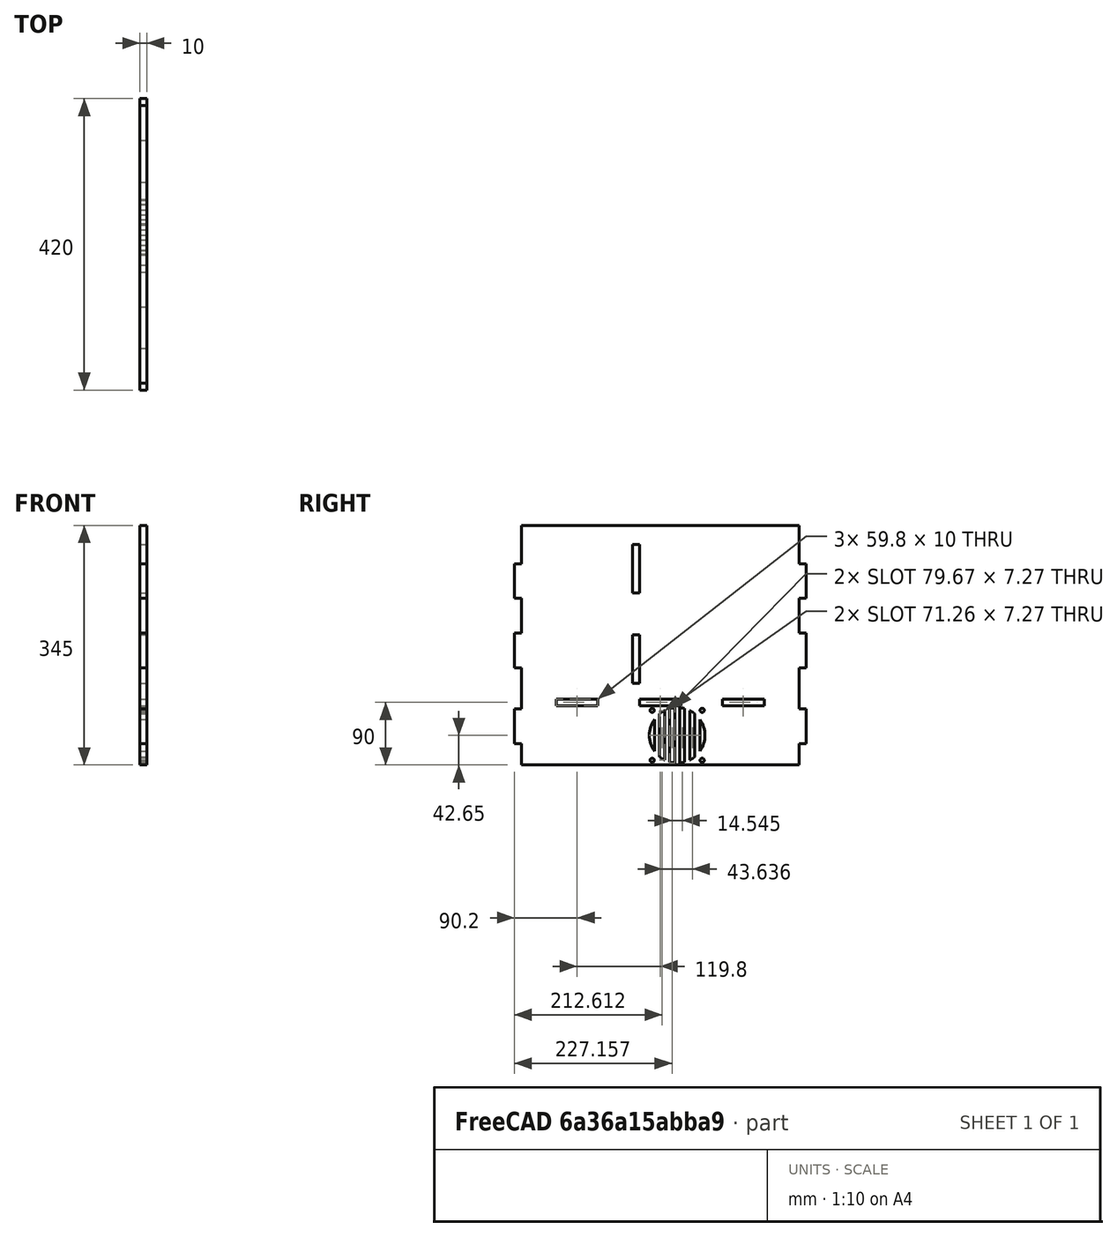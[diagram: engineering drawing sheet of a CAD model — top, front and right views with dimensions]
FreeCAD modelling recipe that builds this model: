
FCSTD DOCUMENT  (FreeCAD 0.19R19327 (Git))
Label: Trasera
License: All rights reserved
LicenseURL: http://en.wikipedia.org/wiki/All_rights_reserved
objects: Sketcher::SketchObject×1, PartDesign::Pad×1, PartDesign::Body×1
note: 4 computed .brp shape members not serialized (recipe doc carries the construction recipe); baked Part::Feature solids carry a one-line shape summary decoded from their .brp

FEATURE [Sketcher::SketchObject] Sketch
  MapMode = 5
  Placement = pos=(0,0,0) rot=(0.57735,0.57735,0.57735;2.0944rad)
  Support = -> [YZ_Plane]
  sketch-geometry (93):
    g0: LineSegment StartX=0 StartY=0 StartZ=0 EndX=0 EndY=30.83 EndZ=0
    g1: LineSegment StartX=0 StartY=30.83 StartZ=0 EndX=-10 EndY=30.83 EndZ=0
    g2: LineSegment StartX=-10 StartY=30.83 StartZ=0 EndX=-10 EndY=80.83 EndZ=0
    g3: LineSegment StartX=-10 StartY=80.83 StartZ=0 EndX=0 EndY=80.83 EndZ=0
    g4: LineSegment StartX=0 StartY=80.83 StartZ=0 EndX=0 EndY=140.1 EndZ=0
    g5: LineSegment StartX=0 StartY=140.1 StartZ=0 EndX=-10 EndY=140.1 EndZ=0
    g6: LineSegment StartX=-10 StartY=140.1 StartZ=0 EndX=-10 EndY=190.1 EndZ=0
    g7: LineSegment StartX=-10 StartY=190.1 StartZ=0 EndX=0 EndY=190.1 EndZ=0
    g8: LineSegment StartX=0 StartY=190.1 StartZ=0 EndX=0 EndY=239.9 EndZ=0
    g9: LineSegment StartX=0 StartY=239.9 StartZ=0 EndX=-10 EndY=239.9 EndZ=0
    g10: LineSegment StartX=-10 StartY=239.9 StartZ=0 EndX=-10 EndY=289.9 EndZ=0
    g11: LineSegment StartX=-10 StartY=289.9 StartZ=0 EndX=0 EndY=289.9 EndZ=0
    g12: LineSegment StartX=0 StartY=289.9 StartZ=0 EndX=0 EndY=345 EndZ=0
    g13: LineSegment StartX=0 StartY=345 StartZ=0 EndX=400 EndY=345 EndZ=0
    g14: LineSegment StartX=400 StartY=345 StartZ=0 EndX=400 EndY=289.9 EndZ=0
    g15: LineSegment StartX=400 StartY=289.9 StartZ=0 EndX=410 EndY=289.9 EndZ=0
    g16: LineSegment StartX=410 StartY=289.9 StartZ=0 EndX=410 EndY=239.9 EndZ=0
    g17: LineSegment StartX=410 StartY=239.9 StartZ=0 EndX=400 EndY=239.9 EndZ=0
    g18: LineSegment StartX=400 StartY=239.9 StartZ=0 EndX=400 EndY=190.1 EndZ=0
    g19: LineSegment StartX=400 StartY=190.1 StartZ=0 EndX=410 EndY=190.1 EndZ=0
    g20: LineSegment StartX=410 StartY=190.1 StartZ=0 EndX=410 EndY=140.1 EndZ=0
    g21: LineSegment StartX=410 StartY=140.1 StartZ=0 EndX=400 EndY=140.1 EndZ=0
    g22: LineSegment StartX=400 StartY=140.1 StartZ=0 EndX=400 EndY=80.83 EndZ=0
    g23: LineSegment StartX=400 StartY=80.83 StartZ=0 EndX=410 EndY=80.83 EndZ=0
    g24: LineSegment StartX=410 StartY=80.83 StartZ=0 EndX=410 EndY=30.83 EndZ=0
    g25: LineSegment StartX=410 StartY=30.83 StartZ=0 EndX=400 EndY=30.83 EndZ=0
    g26: LineSegment StartX=400 StartY=30.83 StartZ=0 EndX=400 EndY=0 EndZ=0
    g27: LineSegment StartX=400 StartY=0 StartZ=0 EndX=0 EndY=0 EndZ=0
    g28: LineSegment StartX=50.3 StartY=95 StartZ=0 EndX=110.1 EndY=95 EndZ=0
    g29: LineSegment StartX=110.1 StartY=95 StartZ=0 EndX=110.1 EndY=85 EndZ=0
    g30: LineSegment StartX=110.1 StartY=85 StartZ=0 EndX=50.3 EndY=85 EndZ=0
    g31: LineSegment StartX=50.3 StartY=85 StartZ=0 EndX=50.3 EndY=95 EndZ=0
    g32: LineSegment StartX=170.1 StartY=95 StartZ=0 EndX=229.9 EndY=95 EndZ=0
    g33: LineSegment StartX=229.9 StartY=95 StartZ=0 EndX=229.9 EndY=85 EndZ=0
    g34: LineSegment StartX=229.9 StartY=85 StartZ=0 EndX=170.1 EndY=85 EndZ=0
    g35: LineSegment StartX=170.1 StartY=85 StartZ=0 EndX=170.1 EndY=95 EndZ=0
    g36: LineSegment StartX=289.9 StartY=95 StartZ=0 EndX=349.7 EndY=95 EndZ=0
    g37: LineSegment StartX=349.7 StartY=95 StartZ=0 EndX=349.7 EndY=85 EndZ=0
    g38: LineSegment StartX=349.7 StartY=85 StartZ=0 EndX=289.9 EndY=85 EndZ=0
    g39: LineSegment StartX=289.9 StartY=85 StartZ=0 EndX=289.9 EndY=95 EndZ=0
    g40: LineSegment [constr] StartX=-5e-16 StartY=85 StartZ=0 EndX=50.3 EndY=85 EndZ=0
    g41: LineSegment [constr] StartX=110.1 StartY=85 StartZ=0 EndX=170.1 EndY=85 EndZ=0
    g42: LineSegment [constr] StartX=229.9 StartY=85 StartZ=0 EndX=289.9 EndY=85 EndZ=0
    g43: LineSegment [constr] StartX=349.7 StartY=85 StartZ=0 EndX=400 EndY=85 EndZ=0
    g44: LineSegment StartX=160 StartY=317.4 StartZ=0 EndX=170 EndY=317.4 EndZ=0
    g45: LineSegment StartX=170 StartY=317.4 StartZ=0 EndX=170 EndY=247.6 EndZ=0
    g46: LineSegment StartX=170 StartY=247.6 StartZ=0 EndX=160 EndY=247.6 EndZ=0
    g47: LineSegment StartX=160 StartY=247.6 StartZ=0 EndX=160 EndY=317.4 EndZ=0
    g48: LineSegment StartX=160 StartY=187.4 StartZ=0 EndX=170 EndY=187.4 EndZ=0
    g49: LineSegment StartX=170 StartY=187.4 StartZ=0 EndX=170 EndY=117.6 EndZ=0
    g50: LineSegment StartX=170 StartY=117.6 StartZ=0 EndX=160 EndY=117.6 EndZ=0
    g51: LineSegment StartX=160 StartY=117.6 StartZ=0 EndX=160 EndY=187.4 EndZ=0
    g52: LineSegment [constr] StartX=160 StartY=187.4 StartZ=0 EndX=160 EndY=247.6 EndZ=0
    g53: LineSegment [constr] StartX=188.43 StartY=78.65 StartZ=0 EndX=260.43 EndY=78.65 EndZ=0
    g54: LineSegment [constr] StartX=260.43 StartY=78.65 StartZ=0 EndX=260.43 EndY=6.65 EndZ=0
    g55: LineSegment [constr] StartX=260.43 StartY=6.65 StartZ=0 EndX=188.43 EndY=6.65 EndZ=0
    g56: LineSegment [constr] StartX=188.43 StartY=6.65 StartZ=0 EndX=188.43 EndY=78.65 EndZ=0
    g57: Circle CenterX=188.43 CenterY=6.65 CenterZ=0 NormalX=0 NormalY=0 NormalZ=1 AngleXU=0 Radius=3
    g58: Circle CenterX=260.43 CenterY=6.65 CenterZ=0 NormalX=0 NormalY=0 NormalZ=1 AngleXU=0 Radius=3
    g59: Circle CenterX=260.43 CenterY=78.65 CenterZ=0 NormalX=0 NormalY=0 NormalZ=1 AngleXU=0 Radius=3
    g60: Circle CenterX=188.43 CenterY=78.65 CenterZ=0 NormalX=0 NormalY=0 NormalZ=1 AngleXU=0 Radius=3
    g61: LineSegment [constr] StartX=188.43 StartY=6.65 StartZ=0 EndX=260.43 EndY=78.65 EndZ=0
    g62: ArcOfCircle CenterX=224.43 CenterY=42.65 CenterZ=0 NormalX=0 NormalY=0 NormalZ=1 AngleXU=0 Radius=40 StartAngle=2.52904 EndAngle=3.75415
    g63: LineSegment StartX=191.703 StartY=19.6516 StartZ=0 EndX=191.703 EndY=65.6484 EndZ=0
    g64: LineSegment StartX=198.975 StartY=11.7944 StartZ=0 EndX=198.975 EndY=73.5056 EndZ=0
    g65: LineSegment StartX=206.248 StartY=7.02106 StartZ=0 EndX=206.248 EndY=78.2789 EndZ=0
    g66: LineSegment StartX=213.521 StartY=4.16634 StartZ=0 EndX=213.521 EndY=81.1337 EndZ=0
    g67: LineSegment StartX=220.794 StartY=2.81563 StartZ=0 EndX=220.794 EndY=82.4844 EndZ=0
    g68: LineSegment [constr] StartX=206.248 StartY=42.65 StartZ=0 EndX=213.521 EndY=42.65 EndZ=0
    g69: LineSegment [constr] StartX=220.794 StartY=42.65 StartZ=0 EndX=228.066 EndY=42.65 EndZ=0
    g70: LineSegment [constr] StartX=191.703 StartY=42.65 StartZ=0 EndX=198.975 EndY=42.65 EndZ=0
    g71: LineSegment StartX=228.066 StartY=2.81563 StartZ=0 EndX=228.066 EndY=82.4844 EndZ=0
    g72: LineSegment StartX=235.339 StartY=4.16634 StartZ=0 EndX=235.339 EndY=81.1337 EndZ=0
    g73: LineSegment StartX=242.612 StartY=7.02106 StartZ=0 EndX=242.612 EndY=78.2789 EndZ=0
    g74: LineSegment StartX=249.885 StartY=73.5056 StartZ=0 EndX=249.885 EndY=11.7944 EndZ=0
    g75: LineSegment StartX=257.157 StartY=19.6516 StartZ=0 EndX=257.157 EndY=65.6484 EndZ=0
    g76: LineSegment [constr] StartX=235.339 StartY=42.65 StartZ=0 EndX=242.612 EndY=42.65 EndZ=0
    g77: LineSegment [constr] StartX=249.885 StartY=42.65 StartZ=0 EndX=257.157 EndY=42.65 EndZ=0
    g78: LineSegment [constr] StartX=184.43 StartY=42.65 StartZ=0 EndX=191.703 EndY=42.65 EndZ=0
    g79: LineSegment [constr] StartX=198.975 StartY=42.65 StartZ=0 EndX=206.248 EndY=42.65 EndZ=0
    g80: LineSegment [constr] StartX=213.521 StartY=42.65 StartZ=0 EndX=220.794 EndY=42.65 EndZ=0
    g81: LineSegment [constr] StartX=228.066 StartY=42.65 StartZ=0 EndX=235.339 EndY=42.65 EndZ=0
    g82: LineSegment [constr] StartX=242.612 StartY=42.65 StartZ=0 EndX=249.885 EndY=42.65 EndZ=0
    g83: LineSegment [constr] StartX=257.157 StartY=42.65 StartZ=0 EndX=264.43 EndY=42.65 EndZ=0
    g84: ArcOfCircle CenterX=224.43 CenterY=42.65 CenterZ=0 NormalX=0 NormalY=0 NormalZ=1 AngleXU=0 Radius=40 StartAngle=4.02261 EndAngle=4.24053
    g85: ArcOfCircle CenterX=224.43 CenterY=42.65 CenterZ=0 NormalX=0 NormalY=0 NormalZ=1 AngleXU=0 Radius=40 StartAngle=4.43616 EndAngle=4.62135
    g86: ArcOfCircle CenterX=224.43 CenterY=42.65 CenterZ=0 NormalX=0 NormalY=0 NormalZ=1 AngleXU=0 Radius=40 StartAngle=2.04266 EndAngle=2.26057
    g87: ArcOfCircle CenterX=224.43 CenterY=42.65 CenterZ=0 NormalX=0 NormalY=0 NormalZ=1 AngleXU=0 Radius=40 StartAngle=1.66183 EndAngle=1.84702
    g88: ArcOfCircle CenterX=224.43 CenterY=42.65 CenterZ=0 NormalX=0 NormalY=0 NormalZ=1 AngleXU=0 Radius=40 StartAngle=4.80342 EndAngle=4.98862
    g89: ArcOfCircle CenterX=224.43 CenterY=42.65 CenterZ=0 NormalX=0 NormalY=0 NormalZ=1 AngleXU=0 Radius=40 StartAngle=5.18425 EndAngle=5.40216
    g90: ArcOfCircle CenterX=224.43 CenterY=42.65 CenterZ=0 NormalX=0 NormalY=0 NormalZ=1 AngleXU=0 Radius=40 StartAngle=5.67063 EndAngle=6.89574
    g91: ArcOfCircle CenterX=224.43 CenterY=42.65 CenterZ=0 NormalX=0 NormalY=0 NormalZ=1 AngleXU=0 Radius=40 StartAngle=0.881021 EndAngle=1.09893
    g92: ArcOfCircle CenterX=224.43 CenterY=42.65 CenterZ=0 NormalX=0 NormalY=0 NormalZ=1 AngleXU=0 Radius=40 StartAngle=1.29457 EndAngle=1.47976
  constraints (286):
    c: Coincident(g-1,g0)
    c: PointOnObject(g0,g-2)
    c: Coincident(g0,g1)
    c: Horizontal(g1)
    c: Coincident(g1,g2)
    c: Vertical(g2)
    c: Coincident(g2,g3)
    c: Horizontal(g3)
    c: Coincident(g3,g4)
    c: Vertical(g4)
    c: Coincident(g4,g5)
    c: Coincident(g5,g6)
    c: Vertical(g6)
    c: Coincident(g6,g7)
    c: Horizontal(g7)
    c: Coincident(g7,g8)
    c: Vertical(g8)
    c: Coincident(g8,g9)
    c: Horizontal(g9)
    c: Coincident(g9,g10)
    c: Vertical(g10)
    c: Coincident(g10,g11)
    c: Horizontal(g11)
    c: Coincident(g11,g12)
    c: PointOnObject(g12,g-2)
    c: Coincident(g12,g13)
    c: Horizontal(g13)
    c: Coincident(g13,g14)
    c: Vertical(g14)
    c: Coincident(g14,g15)
    c: Coincident(g15,g16)
    c: Vertical(g16)
    c: Coincident(g16,g17)
    c: Horizontal(g17)
    c: Coincident(g17,g18)
    c: Vertical(g18)
    c: Coincident(g18,g19)
    c: Coincident(g19,g20)
    c: Coincident(g20,g21)
    c: Coincident(g21,g22)
    c: Vertical(g22)
    c: Coincident(g22,g23)
    c: Coincident(g23,g24)
    c: Vertical(g24)
    c: Coincident(g24,g25)
    c: Coincident(g25,g26)
    c: PointOnObject(g26,g-1)
    c: Vertical(g26)
    c: Coincident(g26,g27)
    c: Coincident(g27,g0)
    c: Horizontal(g5)
    c: Equal(g1,g3)
    c: Equal(g3,g5)
    c: Equal(g5,g7)
    c: Equal(g7,g9)
    c: Equal(g9,g11)
    c: Equal(g11,g15)
    c: Equal(g15,g17)
    c: Equal(g17,g19)
    c: Equal(g19,g21)
    c: Equal(g21,g23)
    c: Equal(g23,g25)
    c: Horizontal(g25)
    c: Horizontal(g23)
    c: Horizontal(g21)
    c: Vertical(g20)
    c: Horizontal(g15)
    c: DistanceX(g1,g1) = 10
    c: Equal(g2,g6)
    c: Equal(g6,g10)
    c: Equal(g10,g24)
    c: Equal(g24,g20)
    c: Equal(g20,g16)
    c: DistanceY(g2,g2) = 50
    c: DistanceY(g12,g12) = 55.1
    c: Equal(g12,g14)
    c: Equal(g0,g26)
    c: DistanceY(g0,g0) = 30.83
    c: DistanceX(g13,g13) = 400
    c: DistanceY(g4,g4) = 59.27
    c: Coincident(g28,g29)
    c: Coincident(g29,g30)
    c: Coincident(g30,g31)
    c: Coincident(g31,g28)
    c: Horizontal(g28)
    c: Horizontal(g30)
    c: Vertical(g29)
    c: Vertical(g31)
    c: Coincident(g32,g33)
    c: Coincident(g33,g34)
    c: Coincident(g34,g35)
    c: Coincident(g35,g32)
    c: Horizontal(g32)
    c: Horizontal(g34)
    c: Vertical(g33)
    c: Vertical(g35)
    c: Coincident(g36,g37)
    c: Coincident(g37,g38)
    c: Coincident(g38,g39)
    c: Coincident(g39,g36)
    c: Horizontal(g36)
    c: Horizontal(g38)
    c: Vertical(g37)
    c: Vertical(g39)
    c: Equal(g28,g32)
    c: Equal(g32,g36)
    c: Equal(g39,g35)
    c: Equal(g35,g31)
    c: PointOnObject(g40,g4)
    c: Horizontal(g40)
    c: Coincident(g30,g40)
    c: Coincident(g41,g29)
    c: Horizontal(g41)
    c: Coincident(g34,g41)
    c: Coincident(g42,g33)
    c: Horizontal(g42)
    c: Coincident(g38,g42)
    c: Coincident(g43,g37)
    c: PointOnObject(g43,g22)
    c: Horizontal(g43)
    c: Equal(g43,g40)
    c: Equal(g41,g42)
    c: Coincident(g44,g45)
    c: Coincident(g45,g46)
    c: Coincident(g46,g47)
    c: Coincident(g47,g44)
    c: Horizontal(g44)
    c: Horizontal(g46)
    c: Vertical(g45)
    c: Vertical(g47)
    c: Coincident(g48,g49)
    c: Coincident(g49,g50)
    c: Coincident(g50,g51)
    c: Coincident(g51,g48)
    c: Horizontal(g48)
    c: Horizontal(g50)
    c: Vertical(g49)
    c: Equal(g51,g47)
    c: Equal(g44,g48)
    c: Equal(g31,g50)
    c: Equal(g50,g46)
    c: DistanceX(g48,g48) = 10
    c: DistanceX(g28,g28) = 59.8
    c: DistanceX(g40,g40) = 50.3
    c: DistanceY(g0,g30) = 85
    c: Coincident(g52,g48)
    c: Vertical(g52)
    c: Coincident(g46,g52)
    c: DistanceY(g52,g52) = 60.2
    c: DistanceY(g51,g51) = 69.8
    c: DistanceY(g0,g50) = 117.6
    c: DistanceX(g0,g50) = 160
    c: Coincident(g53,g54)
    c: Coincident(g54,g55)
    c: Coincident(g55,g56)
    c: Coincident(g56,g53)
    c: Horizontal(g53)
    c: Horizontal(g55)
    c: Vertical(g54)
    c: Vertical(g56)
    c: Equal(g55,g54)
    c: DistanceX(g55,g55) = 72
    c: Coincident(g57,g55)
    c: Coincident(g58,g54)
    c: Coincident(g59,g53)
    c: Coincident(g60,g53)
    c: Equal(g60,g59)
    c: Equal(g59,g57)
    c: Equal(g57,g58)
    c: Radius(g60) = 3
    c: DistanceX(g0,g57) = 188.43
    c: DistanceY(g0,g57) = 6.65
    c: Coincident(g61,g57)
    c: Coincident(g61,g59)
    c: Symmetric(g57,g59,g62)
    c: Radius(g62) = 40
    c: Vertical(g63)
    c: Vertical(g64)
    c: Vertical(g65)
    c: Vertical(g66)
    c: Vertical(g67)
    c: PointOnObject(g64,g62)
    c: PointOnObject(g65,g62)
    c: PointOnObject(g66,g62)
    c: PointOnObject(g66,g62)
    c: PointOnObject(g67,g62)
    c: PointOnObject(g67,g62)
    c: PointOnObject(g68,g65)
    c: PointOnObject(g68,g66)
    c: Horizontal(g68)
    c: PointOnObject(g69,g67)
    c: Horizontal(g69)
    c: PointOnObject(g70,g64)
    c: Horizontal(g70)
    c: Equal(g70,g68)
    c: Equal(g68,g69)
    c: Vertical(g71)
    c: Vertical(g72)
    c: Vertical(g73)
    c: PointOnObject(g71,g62)
    c: PointOnObject(g71,g62)
    c: PointOnObject(g72,g62)
    c: PointOnObject(g73,g62)
    c: PointOnObject(g72,g62)
    c: PointOnObject(g73,g62)
    c: PointOnObject(g69,g71)
    c: Vertical(g74)
    c: Vertical(g75)
    c: PointOnObject(g74,g62)
    c: PointOnObject(g74,g62)
    c: PointOnObject(g75,g62)
    c: PointOnObject(g75,g62)
    c: PointOnObject(g76,g72)
    c: PointOnObject(g76,g73)
    c: Horizontal(g76)
    c: PointOnObject(g77,g74)
    c: PointOnObject(g77,g75)
    c: Horizontal(g77)
    c: Equal(g77,g76)
    c: Equal(g76,g69)
    c: PointOnObject(g78,g62)
    c: Horizontal(g78)
    c: Horizontal(g79)
    c: Horizontal(g80)
    c: Horizontal(g81)
    c: Horizontal(g82)
    c: Horizontal(g83)
    c: PointOnObject(g83,g62)
    c: Equal(g78,g79)
    c: Equal(g79,g80)
    c: Equal(g80,g81)
    c: Equal(g81,g82)
    c: Equal(g82,g83)
    c: Equal(g83,g69)
    c: Coincident(g62,g63)
    c: Coincident(g86,g64)
    c: Equal(g62,g84)
    c: Coincident(g62,g63)
    c: Coincident(g62,g84)
    c: Equal(g84,g85)
    c: PointOnObject(g85,g66)
    c: Coincident(g84,g85)
    c: Equal(g85,g86)
    c: PointOnObject(g87,g66)
    c: Coincident(g85,g86)
    c: Equal(g85,g87)
    c: PointOnObject(g92,g71)
    c: PointOnObject(g87,g67)
    c: Coincident(g85,g87)
    c: Equal(g85,g88)
    c: PointOnObject(g85,g67)
    c: PointOnObject(g88,g71)
    c: Coincident(g85,g88)
    c: Equal(g88,g89)
    c: PointOnObject(g88,g72)
    c: PointOnObject(g89,g73)
    c: Coincident(g88,g89)
    c: Equal(g89,g90)
    c: PointOnObject(g89,g74)
    c: PointOnObject(g90,g75)
    c: Coincident(g89,g90)
    c: Equal(g90,g91)
    c: PointOnObject(g90,g75)
    c: Coincident(g90,g91)
    c: Equal(g91,g92)
    c: PointOnObject(g91,g73)
    c: PointOnObject(g92,g72)
    c: Coincident(g91,g92)
    c: PointOnObject(g91,g74)
    c: Coincident(g70,g78)
    c: Coincident(g79,g70)
    c: Coincident(g68,g79)
    c: Coincident(g80,g68)
    c: Coincident(g80,g69)
    c: Coincident(g69,g81)
    c: Coincident(g81,g76)
    c: Coincident(g82,g76)
    c: Coincident(g77,g82)
    c: Coincident(g83,g77)
    c: Symmetric(g62,g62,g70)
    c: Coincident(g86,g65)
    c: PointOnObject(g84,g65)
    c: PointOnObject(g84,g64)
    c: Horizontal(g19)
    c: DistanceY(g8,g8) = 49.8
    c: Equal(g22,g4)
FEATURE [PartDesign::Pad] Pad
  Length = 10
  Length2 = 100
  Placement = pos=(0,0,0) rot=(0.57735,0.57735,0.57735;2.0944rad)
  Profile = -> Sketch
  Type = 0
FEATURE [PartDesign::Body] Body
  Group = -> [Sketch,Pad]
  Origin = -> Origin
  Tip = -> Pad
